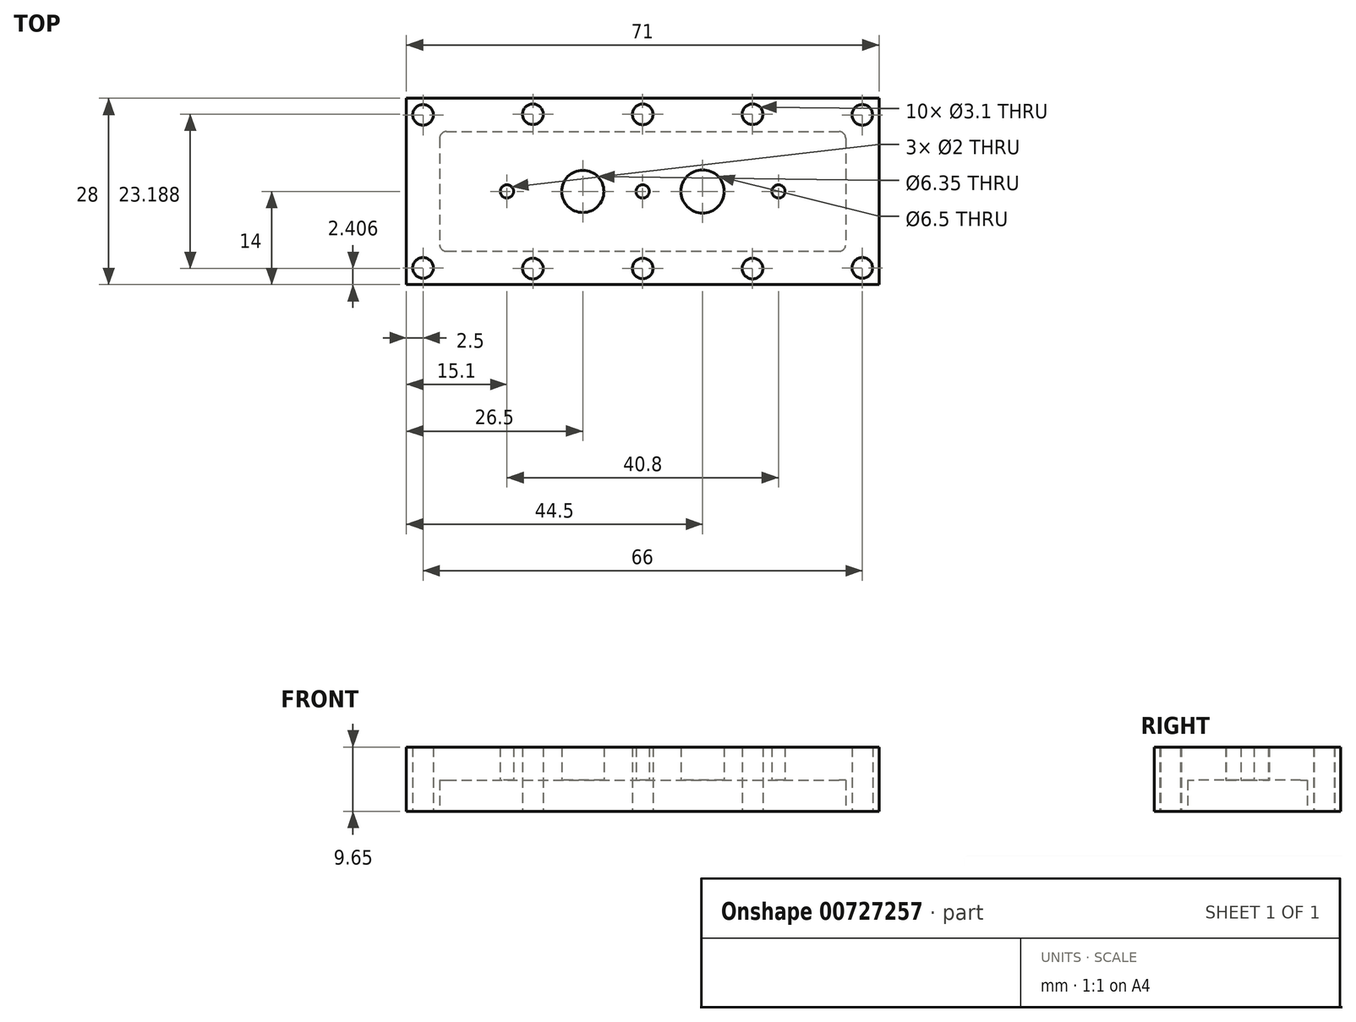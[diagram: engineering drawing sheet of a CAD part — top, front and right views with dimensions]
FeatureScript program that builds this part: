
annotation { "Feature Type Name" : "Feature", "Feature Type Description" : "" }
export const myFeature = defineFeature(function(context is Context, id is Id, definition is map)
    precondition{}
    {
        {
            var Q0;
            Q0=qCreatedBy(makeId("Top.planeOp"),FACE);
            var sketch = newSketch(context, id + "F0", { "sketchPlane" : qUnion([Q0])});
            skLineSegment(sketch, "E0.bottom", {"start": v(-35.5, 14) * mm, "end": v(35.5, 14) * mm});
            skLineSegment(sketch, "E0.top", {"start": v(-35.5, -14) * mm, "end": v(35.5, -14) * mm});
            skLineSegment(sketch, "E0.left", {"start": v(-35.5, 14) * mm, "end": v(-35.5, -14) * mm});
            skLineSegment(sketch, "E0.right", {"start": v(35.5, 14) * mm, "end": v(35.5, -14) * mm});
            skPoint(sketch, "E0.middle", {"position": v(0, 0) * mm});
            skLineSegment(sketch, "E1.bottom", {"start": v(-30.5, 9) * mm, "end": v(30.5, 9) * mm});
            skLineSegment(sketch, "E1.top", {"start": v(-30.5, -9) * mm, "end": v(30.5, -9) * mm});
            skLineSegment(sketch, "E1.left", {"start": v(-30.5, 9) * mm, "end": v(-30.5, -9) * mm});
            skLineSegment(sketch, "E1.right", {"start": v(30.5, 9) * mm, "end": v(30.5, -9) * mm});
            skCircle(sketch, "E2", {"center": v(-20.4, 0) * mm, "radius": 1 * mm});
            skCircle(sketch, "E3", {"center": v(-9, 0) * mm, "radius": 3.17 * mm});
            skCircle(sketch, "E4", {"center": v(20.4, 0) * mm, "radius": 1 * mm});
            skCircle(sketch, "E5", {"center": v(9, 0) * mm, "radius": 3.25 * mm});
            skCircle(sketch, "E6", {"center": v(0, 0) * mm, "radius": 1 * mm});
            skCircle(sketch, "E7", {"center": v(-33, 11.5) * mm, "radius": 1.55 * mm});
            skCircle(sketch, "E8", {"center": v(-16.5, 11.6) * mm, "radius": 1.55 * mm});
            skCircle(sketch, "E9", {"center": v(0, 11.58) * mm, "radius": 1.55 * mm});
            skCircle(sketch, "E10.MirrorC", {"center": v(-33, -11.5) * mm, "radius": 1.55 * mm});
            skCircle(sketch, "E11.MirrorC", {"center": v(33, 11.5) * mm, "radius": 1.55 * mm});
            skCircle(sketch, "E12.MirrorC", {"center": v(33, -11.5) * mm, "radius": 1.55 * mm});
            skCircle(sketch, "E13.MirrorC", {"center": v(-16.5, -11.6) * mm, "radius": 1.55 * mm});
            skCircle(sketch, "E14.MirrorC", {"center": v(16.5, 11.6) * mm, "radius": 1.55 * mm});
            skCircle(sketch, "E15.MirrorC", {"center": v(16.5, -11.6) * mm, "radius": 1.55 * mm});
            skCircle(sketch, "E16.MirrorC", {"center": v(0, -11.58) * mm, "radius": 1.55 * mm});
            skSolve(sketch);
        }
        {
            var Q0;
            Q0=makeQuery(id+"F0.imprint","IMPRINT",FACE,{"disambiguationData":[TD([[makeQuery(id+"F0.imprint","IMPRINT",EDGE,{"derivedFrom":sQuery(id+"F0.wireOp",EDGE,"E0.bottom")}),-1.0]])]});
            var Q1;
            Q1=makeQuery(id+"F0.imprint","IMPRINT",FACE,{"disambiguationData":[TD([[makeQuery(id+"F0.imprint","IMPRINT",EDGE,{"derivedFrom":sQuery(id+"F0.wireOp",EDGE,"E1.bottom")}),-1.0]])]});
            extrude(context, id + "F1", {"entities" : qUnion([Q0, Q1]), "depth" : (5 + 10 - 5.35) * mm, "offsetDistance" : 25 * mm});
        }
        {
            var Q0;
            Q0=makeQuery(id+"F0.imprint","IMPRINT",FACE,{"disambiguationData":[TD([[makeQuery(id+"F0.imprint","IMPRINT",EDGE,{"derivedFrom":sQuery(id+"F0.wireOp",EDGE,"E1.bottom")}),-1.0]])]});
            extrude(context, id + "F2", {"entities" : qUnion([Q0]), "operationType" : NewBodyOperationType.REMOVE, "depth" : (10 - 5.35) * mm, "offsetDistance" : 25 * mm});
        }
        {
            var Q0;
            Q0=makeQuery(id+"F2.boolean.opBoolean","COPY",EDGE,{"derivedFrom":makeQuery(id+"F2.opExtrude","SWEPT_EDGE",EDGE,{"disambiguationData":[OSD([sQuery(id+"F0.wireOp",EDGE,"E1.top"),sQuery(id+"F0.wireOp",EDGE,"E1.left")])]})});
            var Q1;
            Q1=makeQuery(id+"F2.boolean.opBoolean","COPY",EDGE,{"derivedFrom":makeQuery(id+"F2.opExtrude","SWEPT_EDGE",EDGE,{"disambiguationData":[OSD([sQuery(id+"F0.wireOp",EDGE,"E1.top"),sQuery(id+"F0.wireOp",EDGE,"E1.right")])]})});
            var Q2;
            Q2=makeQuery(id+"F2.boolean.opBoolean","COPY",EDGE,{"derivedFrom":makeQuery(id+"F2.opExtrude","SWEPT_EDGE",EDGE,{"disambiguationData":[OSD([sQuery(id+"F0.wireOp",EDGE,"E1.bottom"),sQuery(id+"F0.wireOp",EDGE,"E1.left")])]})});
            var Q3;
            Q3=makeQuery(id+"F2.boolean.opBoolean","COPY",EDGE,{"derivedFrom":makeQuery(id+"F2.opExtrude","SWEPT_EDGE",EDGE,{"disambiguationData":[OSD([sQuery(id+"F0.wireOp",EDGE,"E1.bottom"),sQuery(id+"F0.wireOp",EDGE,"E1.right")])]})});
            fillet(context, id + "F3", {"entities" : qUnion([Q0, Q1, Q2, Q3]), "radius" : 1 * mm, "tangentPropagation" : true, "allowEdgeOverflow" : false});
        }
    });
